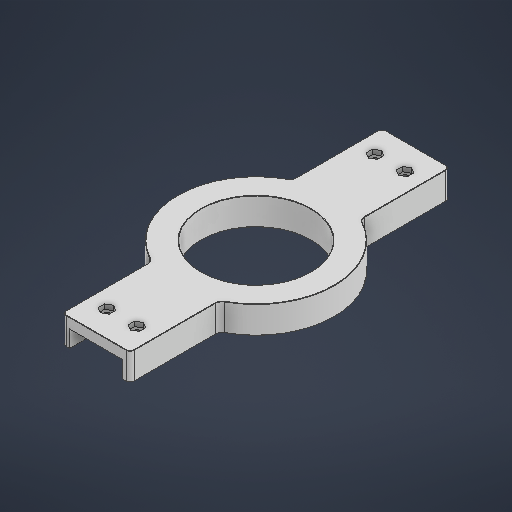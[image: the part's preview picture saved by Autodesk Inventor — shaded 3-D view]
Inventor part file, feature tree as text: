
AUTODESK INVENTOR PART (.ipt)
format: ipt  version: 2025 (Build 290162000, 162)  size: 388,096 bytes
history: native  units: in
note: dims shown in document units (in); Inventor stores cm internally (conversion verified against a paired STEP export)
features: sketch x6, extrude x4, fillet x2, chamfer x1, hole x1
ambient origin geometry x8: Origin, YZ Plane, XZ Plane, XY Plane, X Axis, Y Axis, Z Axis, Center Point
bodies: Solid1 (feature_tree)
feature tree (14):
  extrude  "Extrusion1"  Depth=0.1969in
  fillet  "Fillet1"  Radius=0.7874in
  fillet  "Fillet2"  Radius=0.1969in
  chamfer  "Chamfer1"  Distance=0.0098in Angle=45.0deg
  extrude  "Extrusion4"  Depth=1.5453in
  hole  "Hole2"  [1 undecoded]
  extrude  "Extrusion5"  Depth=0.1181in
  extrude  "Extrusion6"  Depth=0.4951in TaperAngle=0.0deg
  sketch  "Sketch1"  dims[d0=3.1693in d3=4.5276in d4=0.7874in d5=0.0in d28=0.1969in]
  sketch  "Sketch3"  dims[d29=0.1181in d30=0.0098in d31=0.0787in d32=45.0deg]
  sketch  "Sketch4"  dims[d38=1.1122in d39=1.5453in]
  sketch  "Sketch5"  dims[d40=0.1181in d41=0.1181in]
  sketch  "Sketch6"  dims[d42=0.1181in d43=0.4951in d44=0.0in d45=0.748in d48=0.748in d50=0.0935in d51=0.0935in d52=1.7323in d53=1.5453in d55=0.0935in d56=0.0935in d57=0.748in d58=0.748in d59=0.8661in d60=0.8661in d61=0.3396in d62=0.3396in d63=0.1628in d64=0.3937in d65=0.1575in d66=0.0787in d67=90.0deg d68=0.315in d69=0.8108in d70=0.3248in d71=0.3248in d72=0.3248in d73=0.3248in d74=0.1358in d75=0.0in d76=1.9685in d77=2.2638in d78=2.2638in d79=2.5874in d80=2.5874in d81=1.9685in d82=9.252in d83=9.2323in d84=3.7402in d85=0.2756in d86=3.1496in d88=360.0deg d90=0.2756in d91=0.0in d46=0.0344in]
  sketch  "Sketch Circular Pattern3"  dims[d35=1.5453in d37=1.1122in]
note: 1 required parameter value undecoded (feature->parameter linkage not recoverable at this tier; creation-order binding heuristic only, values carry confidence <= 0.55)
